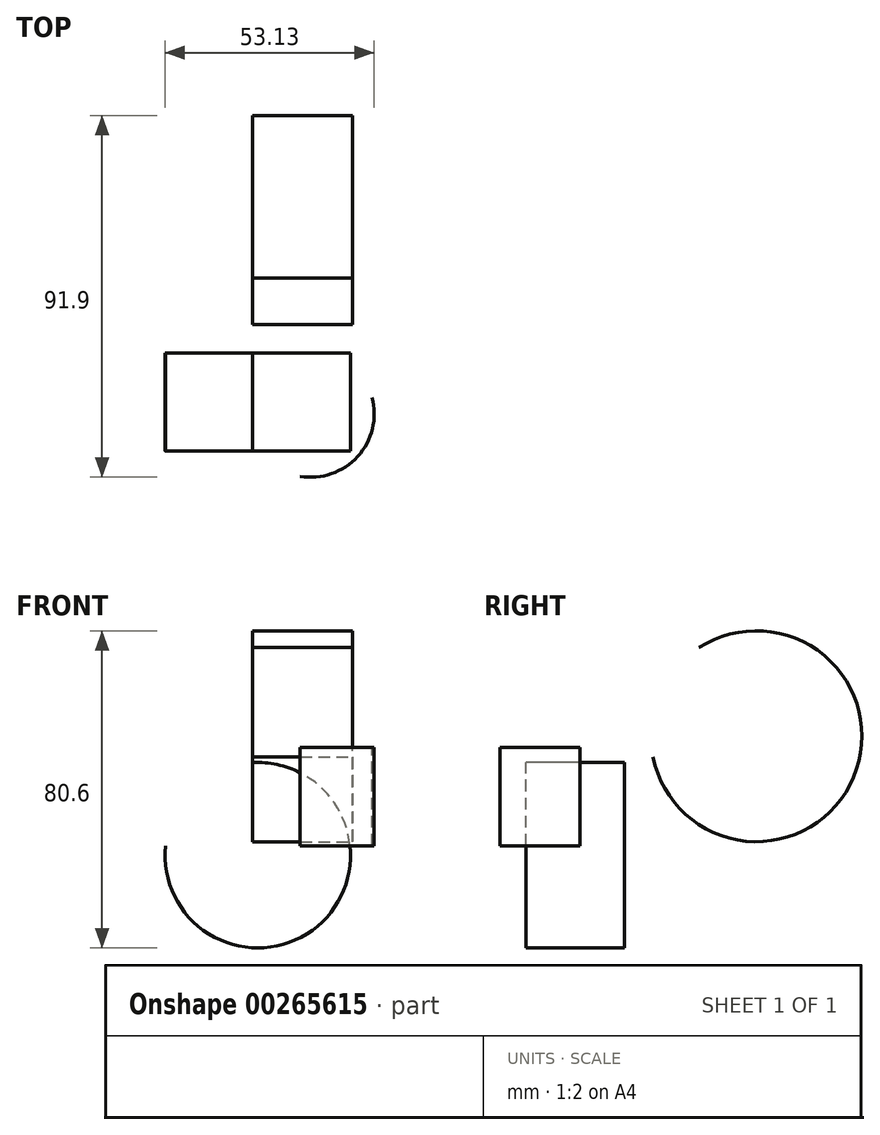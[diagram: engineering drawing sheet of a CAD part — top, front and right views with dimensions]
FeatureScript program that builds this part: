
annotation { "Feature Type Name" : "Feature", "Feature Type Description" : "" }
export const myFeature = defineFeature(function(context is Context, id is Id, definition is map)
    precondition{}
    {
        {
            var Q0;
            Q0=qCreatedBy(makeId("Front.planeOp"),FACE);
            var sketch = newSketch(context, id + "F0", { "sketchPlane" : qUnion([Q0])});
            skArc(sketch, "E0", {"start": v(-22.15, 0) * mm, "mid": v(17.54, -19.48) * mm, "end": v(0, 21.1) * mm});
            skSolve(sketch);
        }
        {
            var Q0;
            Q0=qCreatedBy(makeId("Top.planeOp"),FACE);
            var sketch = newSketch(context, id + "F1", { "sketchPlane" : qUnion([Q0])});
            skArc(sketch, "E1", {"start": v(37.2, 19.18) * mm, "mid": v(34.8, 28.26) * mm, "end": v(26.13, 31.89) * mm});
            skArc(sketch, "E2", {"start": v(30.3, -11.32) * mm, "mid": v(26.67, -26.33) * mm, "end": v(12.07, -31.38) * mm});
            skArc(sketch, "E3", {"start": v(-27.76, -11.8) * mm, "mid": v(-38.1, -10.27) * mm, "end": v(-47.09, -15.61) * mm});
            skSolve(sketch);
        }
        {
            var Q0;
            Q0=qCreatedBy(makeId("Right.planeOp"),FACE);
            var sketch = newSketch(context, id + "F2", { "sketchPlane" : qUnion([Q0])});
            skArc(sketch, "E4", {"start": v(7.22, 22.55) * mm, "mid": v(58.18, 17.4) * mm, "end": v(18.94, 50.32) * mm});
            skSolve(sketch);
        }
        {
            var Q0;
            Q0=sQuery(id+"F2.wireOp",EDGE,"E4");
            extrude(context, id + "F3", {"bodyType" : ToolBodyType.SURFACE, "surfaceEntities" : qUnion([Q0]), "depth" : 25.4 * mm});
        }
        {
            var Q0;
            Q0=sQuery(id+"F1.wireOp",EDGE,"E2");
            extrude(context, id + "F4", {"bodyType" : ToolBodyType.SURFACE, "surfaceEntities" : qUnion([Q0]), "depth" : 25 * mm});
        }
        {
            var Q0;
            Q0=sQuery(id+"F0.wireOp",EDGE,"E0");
            extrude(context, id + "F5", {"bodyType" : ToolBodyType.SURFACE, "surfaceEntities" : qUnion([Q0]), "depth" : 25 * mm});
        }
    });
